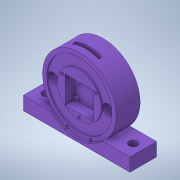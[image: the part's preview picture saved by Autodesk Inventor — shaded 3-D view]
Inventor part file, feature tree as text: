
AUTODESK INVENTOR PART (.ipt)
format: ipt  version: 2020.1 (Build 241239000, 239)  size: 299,008 bytes
history: native  units: in
note: dims shown in document units (in); Inventor stores cm internally (conversion verified against a paired STEP export)
features: sketch x12, extrude x8, hole x6
ambient origin geometry x8: Origin, YZ Plane, XZ Plane, XY Plane, X Axis, Y Axis, Z Axis, Center Point
bodies: Solid1 (feature_tree)
feature tree (26):
  extrude  "Extrusion1"  Depth=0.9in TaperAngle=0.0deg
  extrude  "Extrusion2"  Depth=1.6535in
  extrude  "Extrusion4"  Depth=0.0472in
  extrude  "Extrusion5"  Depth=0.5315in
  extrude  "Extrusion11"  Depth=0.3701in TaperAngle=0.0deg
  extrude  "Extrusion14"  Depth=0.3701in
  extrude  "Extrusion16"  Depth=1.0in TaperAngle=0.0deg
  hole  "Hole for 1/4 0.266 diam"  [1 undecoded]
  hole  "Hole for 1/4 Insert"  [1 undecoded]
  extrude  "Extrusion To Support Camera"  Depth=1.0236in
  hole  "Hole for 2-56 threads for camera"  [1 undecoded]
  hole  "Hole for 2-56 insert"  [1 undecoded]
  hole  "Hole for 6-32 threads for battery holder"  [1 undecoded]
  hole  "Hole20"  [1 undecoded]
  sketch  "Sketch1"  dims[d0=2.7559in d1=0.9in d2=0.0in]
  sketch  "Sketch2"  dims[d3=2.4409in d4=1.6535in]
  sketch  "Sketch7"  dims[d5=0.0472in d6=0.0in d24=0.4119in]
  sketch  "Sketch10"  dims[d25=0.6063in d27=0.5315in]
  sketch  "Sketch20"  dims[d28=0.5315in d31=0.3701in d32=0.0in]
  sketch  "Sketch24"  dims[d33=0.3701in d34=0.4921in]
  sketch  "Sketch27"  dims[d35=0.1339in d36=1.0in d37=0.0in]
  sketch  "Sketch43"  dims[d66=0.164in d76=0.4109in]
  sketch  "Sketch44"  dims[d77=2.0in d78=0.5in]
  sketch  "Sketch45"  dims[d79=0.9in d80=0.0in d95=1.0236in]
  sketch  "Sketch46"  dims[d96=0.3937in d97=0.7874in d99=360.0deg]
  sketch  "Sketch51"  dims[d101=0.2188in d102=0.0in d106=0.1in d107=0.0in d192=0.375in d193=0.375in d194=0.266in d195=0.75in d196=0.507in d197=0.25in d198=0.5635in d199=0.157in d200=0.0in d201=0.316in d202=0.75in d203=0.507in d204=0.25in d205=0.5635in d206=0.312in d207=0.0in d208=0.1063in d209=0.0in d210=0.067in d211=0.172in d212=0.375in d213=0.25in d214=0.5635in d215=0.261in d216=0.0in d217=0.1285in d218=0.172in d219=0.172in d220=0.25in d221=0.5635in d222=0.157in d223=0.0in d224=0.104in d225=0.276in d226=0.191in d227=0.281in d228=0.5635in d229=0.432in d230=0.0in d262=1.4765in d263=1.1811in d265=360.0deg d267=0.104in d268=0.276in d269=0.191in d270=0.281in d271=0.5635in d272=0.432in d273=0.8108in]
note: 6 required parameter values undecoded (feature->parameter linkage not recoverable at this tier; creation-order binding heuristic only, values carry confidence <= 0.55)
